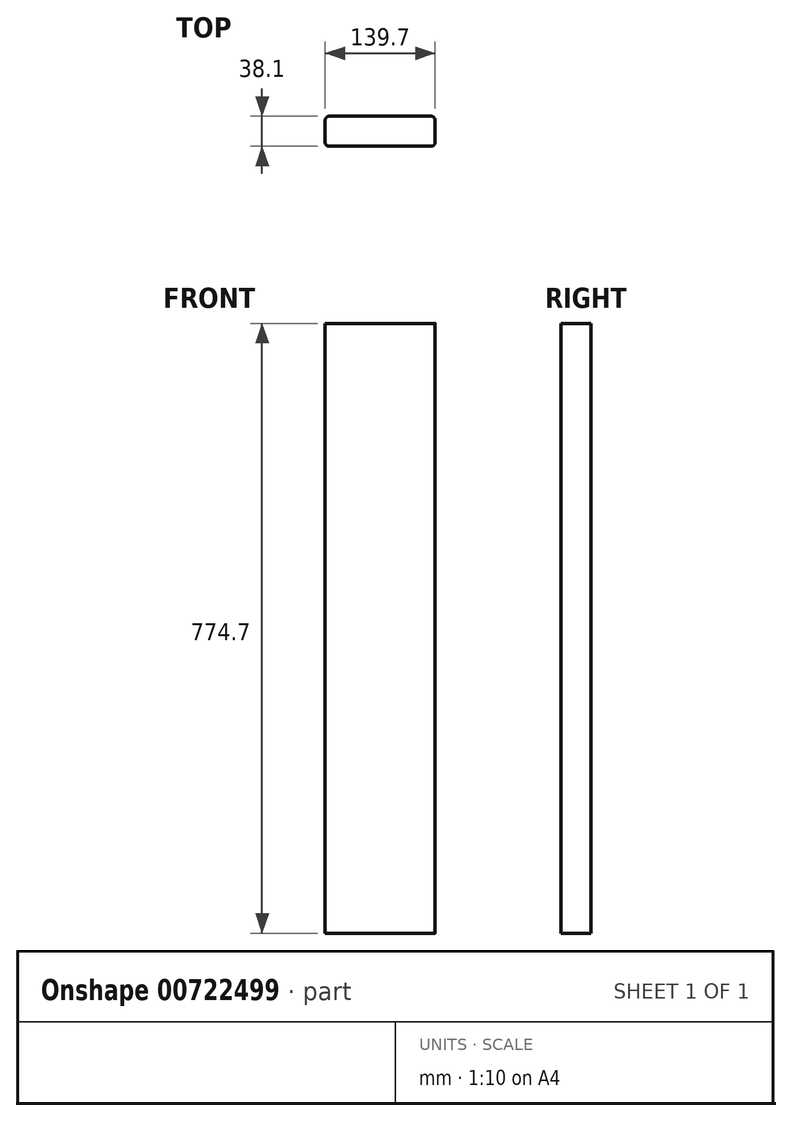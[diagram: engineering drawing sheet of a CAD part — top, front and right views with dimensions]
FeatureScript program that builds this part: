
annotation { "Feature Type Name" : "Feature", "Feature Type Description" : "" }
export const myFeature = defineFeature(function(context is Context, id is Id, definition is map)
    precondition{}
    {
        {
            var Q0;
            Q0=qCreatedBy(makeId("Front.planeOp"),FACE);
            var sketch = newSketch(context, id + "F0", { "sketchPlane" : qUnion([Q0])});
            skLineSegment(sketch, "E0", {"start": v(0, 0) * mm, "end": v(0, -774.7) * mm});
            skLineSegment(sketch, "E1", {"start": v(0, -774.7) * mm, "end": v(139.7, -774.7) * mm});
            skLineSegment(sketch, "E2", {"start": v(139.7, -774.7) * mm, "end": v(139.7, 0) * mm});
            skLineSegment(sketch, "E3", {"start": v(139.7, 0) * mm, "end": v(0, 0) * mm});
            skSolve(sketch);
        }
        {
            var Q0;
            Q0=makeQuery(id+"F0.imprint","IMPRINT",FACE,{"disambiguationData":[TD([[makeQuery(id+"F0.imprint","IMPRINT",EDGE,{"derivedFrom":sQuery(id+"F0.wireOp",EDGE,"E0")}),1.0]])]});
            extrude(context, id + "F1", {"entities" : qUnion([Q0]), "depth" : 38.1 * mm, "offsetDistance" : 25.4 * mm});
        }
        {
            var Q0;
            Q0=makeQuery(id+"F1.opExtrude","CAP_EDGE",EDGE,{"disambiguationData":[OSD([sQuery(id+"F0.wireOp",EDGE,"E2")])],"isStart":true});
            var Q1;
            Q1=makeQuery(id+"F1.opExtrude","CAP_EDGE",EDGE,{"disambiguationData":[OSD([sQuery(id+"F0.wireOp",EDGE,"E0")])],"isStart":true});
            var Q2;
            Q2=makeQuery(id+"F1.opExtrude","CAP_EDGE",EDGE,{"disambiguationData":[OSD([sQuery(id+"F0.wireOp",EDGE,"E2")])],"isStart":false});
            var Q3;
            Q3=makeQuery(id+"F1.opExtrude","CAP_EDGE",EDGE,{"disambiguationData":[OSD([sQuery(id+"F0.wireOp",EDGE,"E0")])],"isStart":false});
            fillet(context, id + "F2", {"entities" : qUnion([Q0, Q1, Q2, Q3]), "radius" : 5.08 * mm, "tangentPropagation" : true, "allowEdgeOverflow" : false});
        }
    });
